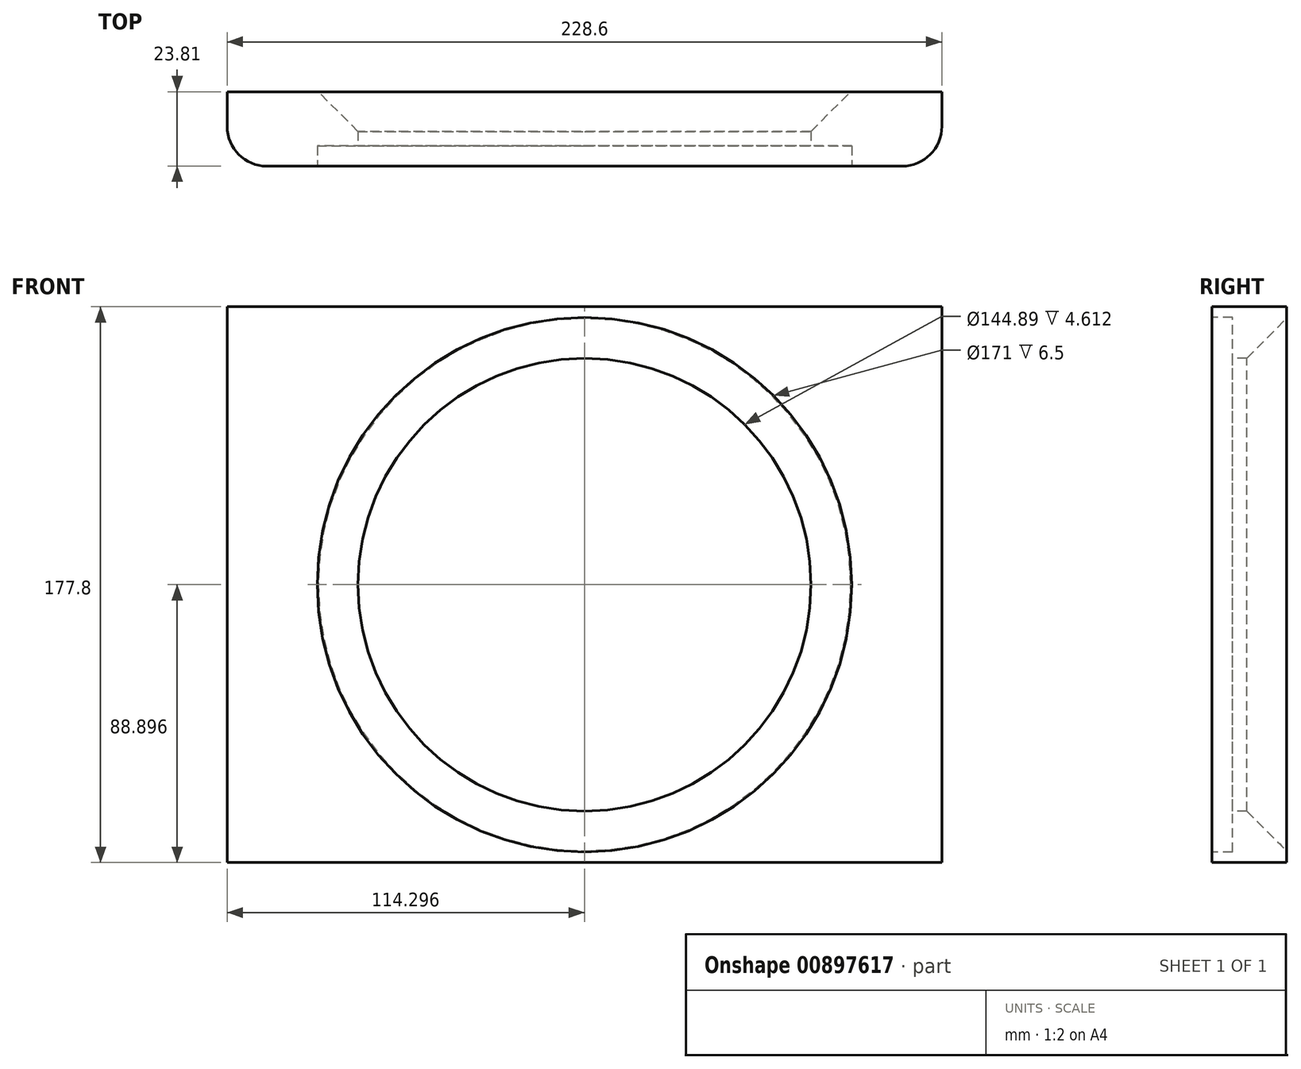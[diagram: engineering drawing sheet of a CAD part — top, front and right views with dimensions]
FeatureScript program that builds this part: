
annotation { "Feature Type Name" : "Feature", "Feature Type Description" : "" }
export const myFeature = defineFeature(function(context is Context, id is Id, definition is map)
    precondition{}
    {
        {
            var Q0;
            Q0=qCreatedBy(makeId("Front.planeOp"),FACE);
            var sketch = newSketch(context, id + "F0", { "sketchPlane" : qUnion([Q0])});
            skLineSegment(sketch, "E0.bottom", {"start": v(-152.83, 64.09) * mm, "end": v(75.77, 64.09) * mm});
            skLineSegment(sketch, "E0.top", {"start": v(-152.83, -113.71) * mm, "end": v(75.77, -113.71) * mm});
            skLineSegment(sketch, "E0.left", {"start": v(-152.83, 64.09) * mm, "end": v(-152.83, -113.71) * mm});
            skLineSegment(sketch, "E0.right", {"start": v(75.77, 64.09) * mm, "end": v(75.77, -113.71) * mm});
            skSolve(sketch);
        }
        {
            var Q0;
            Q0 = qSketchRegion(id + "F0", true);
            extrude(context, id + "F1", {"entities" : qUnion([Q0]), "depth" : 23.8 * mm, "offsetDistance" : 25.4 * mm});
        }
        {
            var Q0;
            Q0=makeQuery(id+"F1.opExtrude","CAP_FACE",FACE,{"disambiguationData":[OSD([sQuery(id+"F0.wireOp",EDGE,"E0.bottom"),sQuery(id+"F0.wireOp",EDGE,"E0.top"),sQuery(id+"F0.wireOp",EDGE,"E0.left"),sQuery(id+"F0.wireOp",EDGE,"E0.right")])],"isStart":false});
            var sketch = newSketch(context, id + "F2", { "sketchPlane" : qUnion([Q0])});
            skLineSegment(sketch, "E1", {"start": v(-152.83, -24.81) * mm, "end": v(75.77, -24.81) * mm, "construction": true});
            skLineSegment(sketch, "E2", {"start": v(-38.53, 64.09) * mm, "end": v(-38.53, -113.71) * mm, "construction": true});
            skCircle(sketch, "E3", {"center": v(-38.53, -24.81) * mm, "radius": 85.5 * mm});
            skCircle(sketch, "E4", {"center": v(-38.53, -24.81) * mm, "radius": 72.44 * mm});
            skSolve(sketch);
        }
        {
            var Q0;
            Q0=makeQuery(id+"F2.imprint","IMPRINT",FACE,{"disambiguationData":[TD([[makeQuery(id+"F2.imprint","IMPRINT",EDGE,{"derivedFrom":sQuery(id+"F2.wireOp",EDGE,"E4")}),1.0]])]});
            extrude(context, id + "F3", {"entities" : qUnion([Q0]), "operationType" : NewBodyOperationType.REMOVE, "oppositeDirection" : true, "depth" : 25.4 * mm, "offsetDistance" : 25.4 * mm});
        }
        {
            var Q0;
            Q0 = qSketchRegion(id + "F2", true);
            extrude(context, id + "F4", {"entities" : qUnion([Q0]), "operationType" : NewBodyOperationType.REMOVE, "oppositeDirection" : true, "depth" : 6.5 * mm, "offsetDistance" : 25.4 * mm});
        }
        {
            var Q0;
            Q0=makeQuery(id+"F1.opExtrude","CAP_EDGE",EDGE,{"disambiguationData":[OSD([sQuery(id+"F0.wireOp",EDGE,"E0.right")])],"isStart":false});
            fillet(context, id + "F5", {"entities" : qUnion([Q0]), "radius" : 12.7 * mm, "tangentPropagation" : true, "allowEdgeOverflow" : false});
        }
        {
            var Q0;
            Q0=makeQuery(id+"F1.opExtrude","CAP_EDGE",EDGE,{"disambiguationData":[OSD([sQuery(id+"F0.wireOp",EDGE,"E0.left")])],"isStart":false});
            fillet(context, id + "F6", {"entities" : qUnion([Q0]), "radius" : 12.7 * mm, "tangentPropagation" : true, "allowEdgeOverflow" : false});
        }
        {
            var Q0;
            Q0=makeQuery(id+"F3.boolean.opBoolean","INTERSECT",EDGE,{"derivedFrom":[makeQuery(id+"F1.opExtrude","CAP_FACE",FACE,{"disambiguationData":[OSD([sQuery(id+"F0.wireOp",EDGE,"E0.bottom"),sQuery(id+"F0.wireOp",EDGE,"E0.top"),sQuery(id+"F0.wireOp",EDGE,"E0.left"),sQuery(id+"F0.wireOp",EDGE,"E0.right")])],"isStart":true}),makeQuery(id+"F3.opExtrude","SWEPT_FACE",FACE,{"disambiguationData":[OSD([sQuery(id+"F2.wireOp",EDGE,"E4")])]})]});
            chamfer(context, id + "F7", {"entities" : qUnion([Q0]), "width" : 12.7 * mm, "tangentPropagation" : true});
        }
    });
